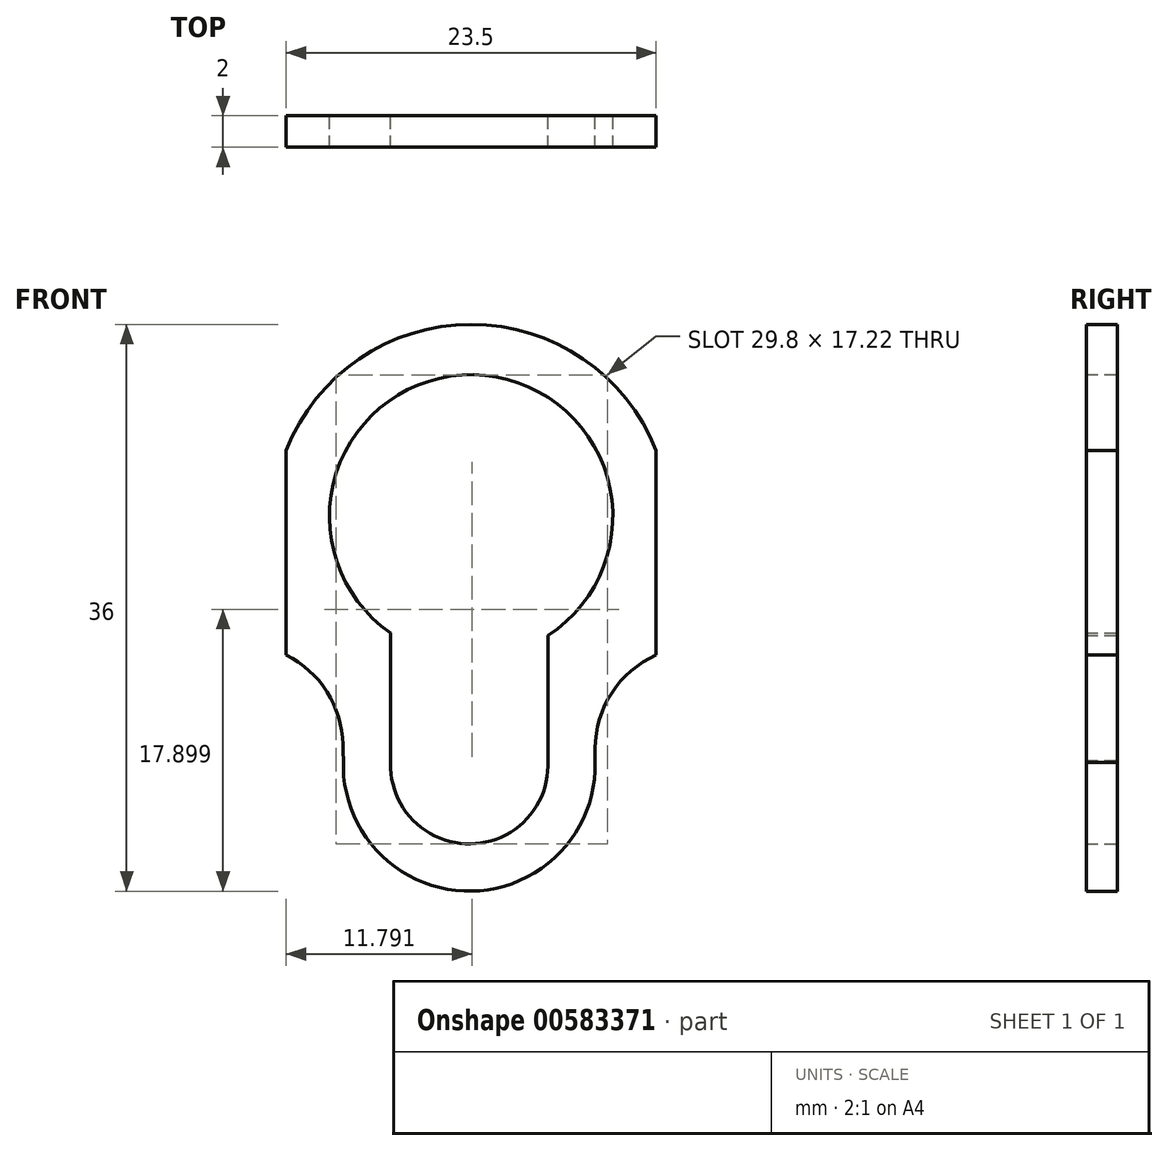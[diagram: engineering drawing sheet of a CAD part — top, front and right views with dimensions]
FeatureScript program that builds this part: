
annotation { "Feature Type Name" : "Feature", "Feature Type Description" : "" }
export const myFeature = defineFeature(function(context is Context, id is Id, definition is map)
    precondition{}
    {
        {
            var Q0;
            Q0=qCreatedBy(makeId("Front.planeOp"),FACE);
            var sketch = newSketch(context, id + "F0", { "sketchPlane" : qUnion([Q0])});
            skLineSegment(sketch, "E0.bottom", {"start": v(-11.63, 0) * mm, "end": v(-8.15, 0) * mm});
            skLineSegment(sketch, "E0.left", {"start": v(-11.63, 0) * mm, "end": v(-11.63, 13) * mm});
            skLineSegment(sketch, "E0.right", {"start": v(11.87, 0) * mm, "end": v(11.87, 13) * mm});
            skArc(sketch, "E1", {"start": v(11.87, 13) * mm, "mid": v(0.12, 21) * mm, "end": v(-11.63, 13) * mm});
            skArc(sketch, "E2", {"start": v(-8, -7.17) * mm, "mid": v(0.17, -15) * mm, "end": v(8, -6.83) * mm});
            skLineSegment(sketch, "E3", {"start": v(-8, -7.17) * mm, "end": v(-8.15, 0) * mm});
            skLineSegment(sketch, "E4", {"start": v(8, -6.83) * mm, "end": v(8, 0) * mm});
            skLineSegment(sketch, "E5.trimOffspring", {"start": v(8, 0) * mm, "end": v(11.87, 0) * mm});
            skArc(sketch, "E6", {"start": v(-5, -6.86) * mm, "mid": v(0.07, -12) * mm, "end": v(5, -6.71) * mm});
            skArc(sketch, "E7", {"start": v(5, 1.23) * mm, "mid": v(0.27, 17.8) * mm, "end": v(-5, 1.4) * mm});
            skLineSegment(sketch, "E8", {"start": v(-5, -7.14) * mm, "end": v(-5, 1.4) * mm});
            skLineSegment(sketch, "E9", {"start": v(5, -6.71) * mm, "end": v(5, 1.23) * mm});
            skSolve(sketch);
        }
        {
            var Q0;
            Q0=makeQuery(id+"F0.imprint","IMPRINT",FACE,{"disambiguationData":[TD([[makeQuery(id+"F0.imprint","IMPRINT",EDGE,{"derivedFrom":sQuery(id+"F0.wireOp",EDGE,"E0.bottom")}),1.0]])]});
            extrude(context, id + "F1", {"entities" : qUnion([Q0]), "depth" : 2 * mm, "offsetDistance" : 25 * mm});
        }
        {
            var Q0;
            Q0=makeQuery(id+"F1.opExtrude","SWEPT_EDGE",EDGE,{"disambiguationData":[OSD([sQuery(id+"F0.wireOp",EDGE,"E0.bottom"),sQuery(id+"F0.wireOp",EDGE,"E3")])]});
            var Q1;
            Q1=makeQuery(id+"F1.opExtrude","SWEPT_EDGE",EDGE,{"disambiguationData":[OSD([sQuery(id+"F0.wireOp",EDGE,"E4"),sQuery(id+"F0.wireOp",EDGE,"E5.trimOffspring")])]});
            fillet(context, id + "F2", {"entities" : qUnion([Q0, Q1]), "radius" : 6.5 * mm, "tangentPropagation" : true, "allowEdgeOverflow" : false});
        }
    });
